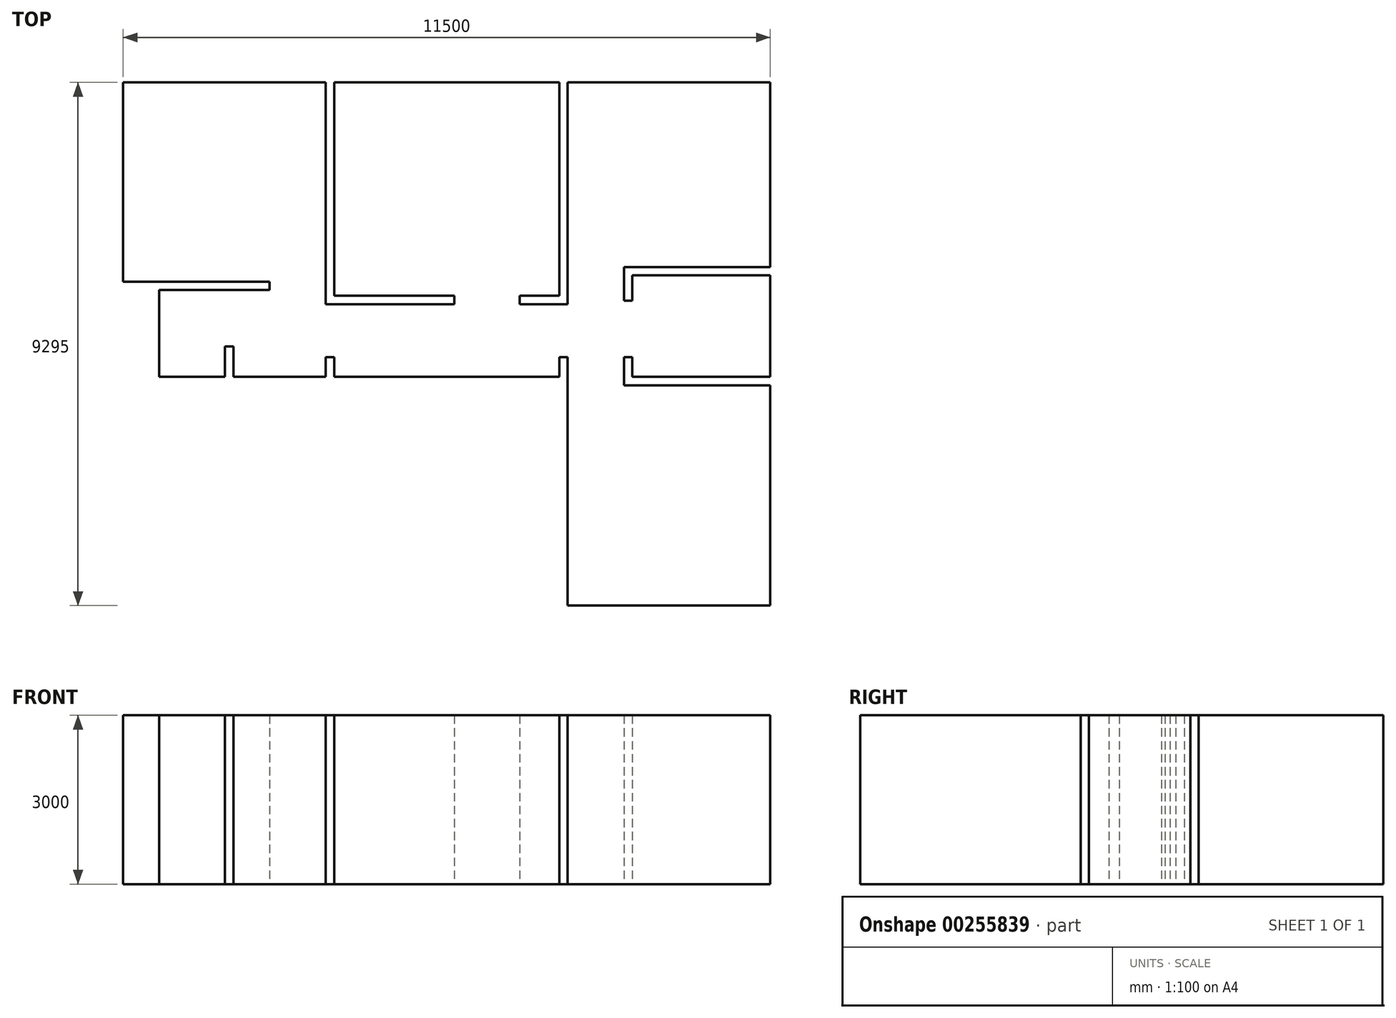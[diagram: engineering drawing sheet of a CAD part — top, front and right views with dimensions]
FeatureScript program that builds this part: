
annotation { "Feature Type Name" : "Feature", "Feature Type Description" : "" }
export const myFeature = defineFeature(function(context is Context, id is Id, definition is map)
    precondition{}
    {
        {
            var Q0;
            Q0=qCreatedBy(makeId("Top.planeOp"),FACE);
            var sketch = newSketch(context, id + "F0", { "sketchPlane" : qUnion([Q0])});
            skLineSegment(sketch, "E0", {"start": v(0, 0) * mm, "end": v(3600, 0) * mm});
            skLineSegment(sketch, "E1", {"start": v(3750, 0) * mm, "end": v(7750, 0) * mm});
            skLineSegment(sketch, "E2", {"start": v(7750, 0) * mm, "end": v(7750, -3790) * mm});
            skLineSegment(sketch, "E3", {"start": v(7750, -3790) * mm, "end": v(7050, -3790) * mm});
            skLineSegment(sketch, "E4", {"start": v(5885.3, -3790) * mm, "end": v(3750, -3790) * mm});
            skLineSegment(sketch, "E5", {"start": v(3750, -3790) * mm, "end": v(3750, 0) * mm});
            skLineSegment(sketch, "E6", {"start": v(5885.3, -3790) * mm, "end": v(5885.3, -3940) * mm});
            skLineSegment(sketch, "E7", {"start": v(5885.3, -3940) * mm, "end": v(3600, -3940) * mm});
            skLineSegment(sketch, "E8", {"start": v(3600, -3940) * mm, "end": v(3600, 0) * mm});
            skLineSegment(sketch, "E9", {"start": v(7050, -3790) * mm, "end": v(7050, -3940) * mm});
            skLineSegment(sketch, "E10", {"start": v(7050, -3940) * mm, "end": v(7750, -3940) * mm});
            skLineSegment(sketch, "E11", {"start": v(7750, -3940) * mm, "end": v(7900, -3940) * mm});
            skLineSegment(sketch, "E12", {"start": v(7900, -3940) * mm, "end": v(7900, 0) * mm});
            skLineSegment(sketch, "E13", {"start": v(7900, 0) * mm, "end": v(11500, 0) * mm});
            skLineSegment(sketch, "E14", {"start": v(11500, 0) * mm, "end": v(11500, -3280) * mm});
            skLineSegment(sketch, "E15", {"start": v(11500, -3430) * mm, "end": v(11500, -5230) * mm});
            skLineSegment(sketch, "E16", {"start": v(11500, -5380) * mm, "end": v(11500, -9295) * mm});
            skLineSegment(sketch, "E17", {"start": v(8900, -3280) * mm, "end": v(11500, -3280) * mm});
            skLineSegment(sketch, "E18", {"start": v(11500, -5380) * mm, "end": v(8900, -5380) * mm});
            skLineSegment(sketch, "E19", {"start": v(8900, -5380) * mm, "end": v(8900, -4880) * mm});
            skLineSegment(sketch, "E20", {"start": v(8900, -3880) * mm, "end": v(8900, -3280) * mm});
            skLineSegment(sketch, "E21", {"start": v(8900, -3880) * mm, "end": v(9050, -3880) * mm});
            skLineSegment(sketch, "E22", {"start": v(8900, -4880) * mm, "end": v(9050, -4880) * mm});
            skLineSegment(sketch, "E23", {"start": v(11500, -3430) * mm, "end": v(9050, -3430) * mm});
            skLineSegment(sketch, "E24", {"start": v(9050, -3430) * mm, "end": v(9050, -3880) * mm});
            skLineSegment(sketch, "E25", {"start": v(11500, -5230) * mm, "end": v(9050, -5230) * mm});
            skLineSegment(sketch, "E26", {"start": v(9050, -5230) * mm, "end": v(9050, -4880) * mm});
            skLineSegment(sketch, "E27", {"start": v(11500, -9295) * mm, "end": v(7900, -9295) * mm});
            skLineSegment(sketch, "E28", {"start": v(7900, -9295) * mm, "end": v(7900, -5380) * mm});
            skLineSegment(sketch, "E29", {"start": v(7900, -5380) * mm, "end": v(7900, -4880) * mm});
            skLineSegment(sketch, "E30", {"start": v(7900, -4880) * mm, "end": v(7750, -4880) * mm});
            skLineSegment(sketch, "E31", {"start": v(7750, -4880) * mm, "end": v(7750, -5230) * mm});
            skLineSegment(sketch, "E32", {"start": v(7750, -5230) * mm, "end": v(3750, -5230) * mm});
            skLineSegment(sketch, "E33", {"start": v(3750, -5230) * mm, "end": v(3750, -4880) * mm});
            skLineSegment(sketch, "E34", {"start": v(0, 0) * mm, "end": v(0, -3540) * mm});
            skLineSegment(sketch, "E35", {"start": v(0, -3540) * mm, "end": v(2600, -3540) * mm});
            skLineSegment(sketch, "E36", {"start": v(2600, -3540) * mm, "end": v(2600, -3690) * mm});
            skLineSegment(sketch, "E37", {"start": v(3600, -5230) * mm, "end": v(3600, -4880) * mm});
            skLineSegment(sketch, "E38", {"start": v(3600, -4880) * mm, "end": v(3750, -4880) * mm});
            skLineSegment(sketch, "E39", {"start": v(3600, -5230) * mm, "end": v(1960, -5230) * mm});
            skLineSegment(sketch, "E40", {"start": v(1810, -5230) * mm, "end": v(640, -5230) * mm});
            skLineSegment(sketch, "E41", {"start": v(640, -5230) * mm, "end": v(640, -3690) * mm});
            skLineSegment(sketch, "E42", {"start": v(640, -3690) * mm, "end": v(2600, -3690) * mm});
            skLineSegment(sketch, "E43", {"start": v(1960, -5230) * mm, "end": v(1960, -4690) * mm});
            skLineSegment(sketch, "E44", {"start": v(1960, -4690) * mm, "end": v(1810, -4690) * mm});
            skLineSegment(sketch, "E45", {"start": v(1810, -4690) * mm, "end": v(1810, -5230) * mm});
            skSolve(sketch);
        }
        {
            var Q0;
            Q0 = qSketchRegion(id + "F0", true);
            extrude(context, id + "F1", {"entities" : qUnion([Q0]), "depth" : 3000 * mm});
        }
    });
